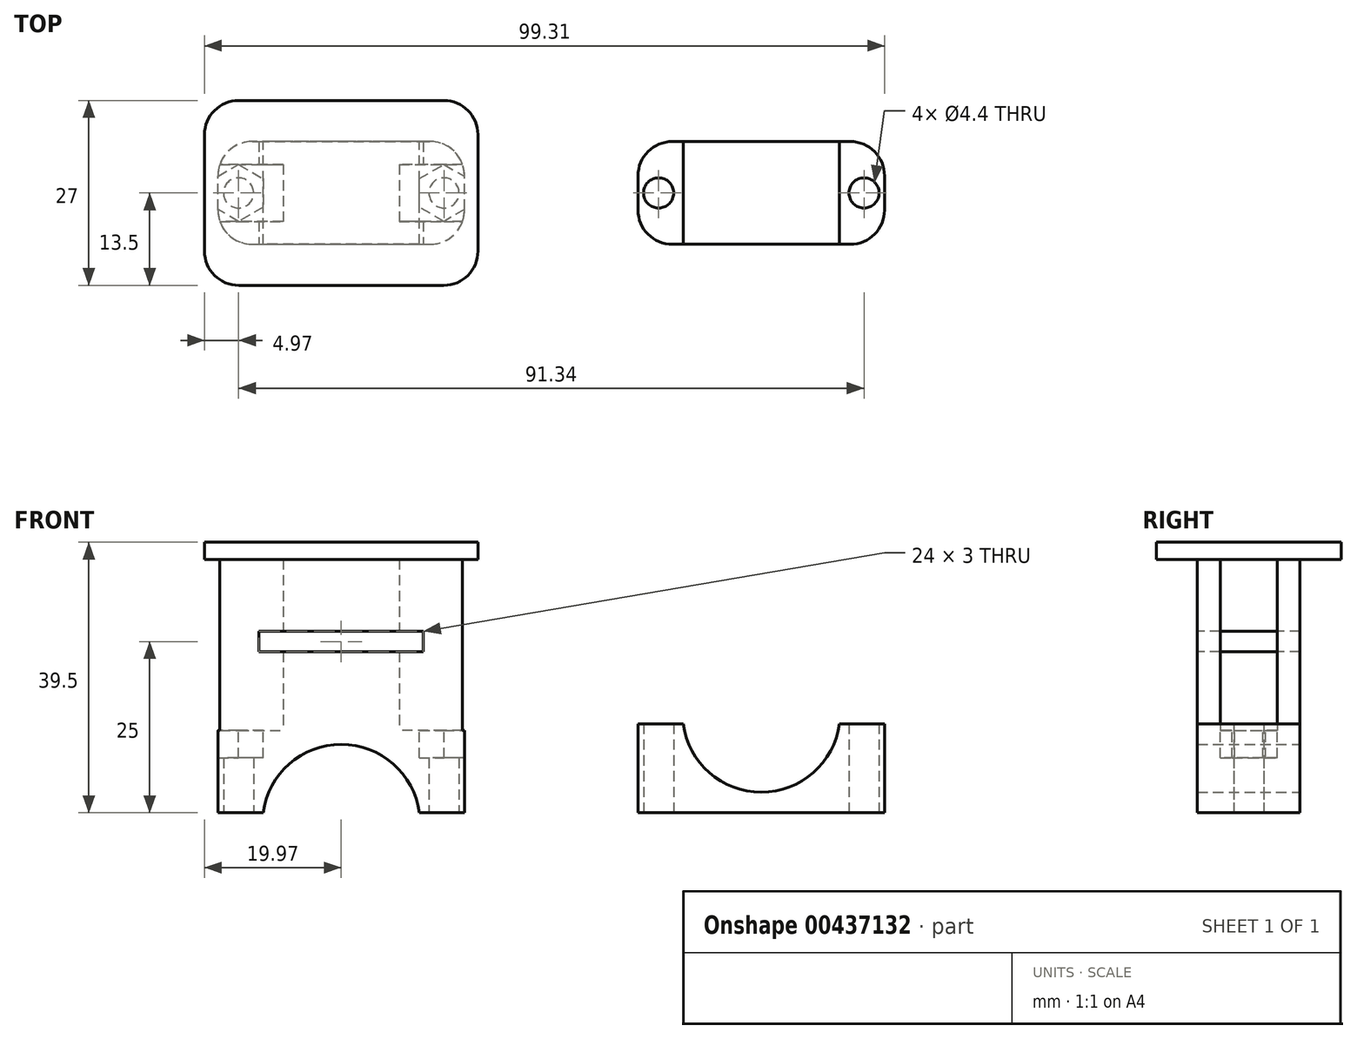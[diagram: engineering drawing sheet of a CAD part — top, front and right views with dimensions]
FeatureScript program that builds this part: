
annotation { "Feature Type Name" : "Feature", "Feature Type Description" : "" }
export const myFeature = defineFeature(function(context is Context, id is Id, definition is map)
    precondition{}
    {
        {
            var Q0;
            Q0=qCreatedBy(makeId("Front.planeOp"),FACE);
            var sketch = newSketch(context, id + "F0", { "sketchPlane" : qUnion([Q0])});
            skLineSegment(sketch, "E0.bottom", {"start": v(0, 0) * mm, "end": v(36, 0) * mm});
            skLineSegment(sketch, "E0.top", {"start": v(0, 13) * mm, "end": v(36, 13) * mm});
            skLineSegment(sketch, "E0.left", {"start": v(0, 0) * mm, "end": v(0, 13) * mm});
            skLineSegment(sketch, "E0.right", {"start": v(36, 0) * mm, "end": v(36, 13) * mm});
            skPoint(sketch, "E1", {"position": v(18, 14.5) * mm});
            skPoint(sketch, "E1.positionSnap0", {"position": v(18, 13) * mm});
            skCircle(sketch, "E2", {"center": v(18, 14.5) * mm, "radius": 11.5 * mm});
            skSolve(sketch);
        }
        {
            var Q0;
            Q0=makeQuery(id+"F0.imprint","IMPRINT",FACE,{"disambiguationData":[TD([[makeQuery(id+"F0.imprint","IMPRINT",EDGE,{"derivedFrom":sQuery(id+"F0.wireOp",EDGE,"E0.bottom")}),1.0]])]});
            extrude(context, id + "F1", {"entities" : qUnion([Q0]), "depth" : 15 * mm});
        }
        {
            var Q0;
            Q0=makeQuery(id+"F1.opExtrude","CAP_EDGE",EDGE,{"disambiguationData":[OSD([sQuery(id+"F0.wireOp",EDGE,"E0.left")])],"isStart":false});
            var Q1;
            Q1=makeQuery(id+"F1.opExtrude","CAP_EDGE",EDGE,{"disambiguationData":[OSD([sQuery(id+"F0.wireOp",EDGE,"E0.right")])],"isStart":false});
            var Q2;
            Q2=makeQuery(id+"F1.opExtrude","CAP_EDGE",EDGE,{"disambiguationData":[OSD([sQuery(id+"F0.wireOp",EDGE,"E0.right")])],"isStart":true});
            var Q3;
            Q3=makeQuery(id+"F1.opExtrude","CAP_EDGE",EDGE,{"disambiguationData":[OSD([sQuery(id+"F0.wireOp",EDGE,"E0.left")])],"isStart":true});
            fillet(context, id + "F2", {"entities" : qUnion([Q0, Q1, Q2, Q3]), "radius" : 5 * mm, "tangentPropagation" : true, "allowEdgeOverflow" : false});
        }
        {
            var Q0;
            Q0=makeQuery(id+"F1.opExtrude","SWEPT_FACE",FACE,{"disambiguationData":[OSD([sQuery(id+"F0.wireOp",EDGE,"E0.bottom")])]});
            var sketch = newSketch(context, id + "F3", { "sketchPlane" : qUnion([Q0])});
            skPoint(sketch, "E3", {"position": v(3, 7.5) * mm});
            skPoint(sketch, "E3.positionSnap0", {"position": v(0, 7.5) * mm});
            skPoint(sketch, "E4", {"position": v(36, 7.5) * mm});
            skPoint(sketch, "E5", {"position": v(33, 7.5) * mm});
            skCircle(sketch, "E6", {"center": v(3, 7.5) * mm, "radius": 2.2 * mm});
            skCircle(sketch, "E7", {"center": v(33, 7.5) * mm, "radius": 2.2 * mm});
            skSolve(sketch);
        }
        {
            var Q0;
            Q0 = qSketchRegion(id + "F3", true);
            extrude(context, id + "F4", {"entities" : qUnion([Q0]), "operationType" : NewBodyOperationType.REMOVE, "oppositeDirection" : true, "depth" : 25 * mm});
        }
        {
            var Q0;
            Q0=qCreatedBy(makeId("Front.planeOp"),FACE);
            var sketch = newSketch(context, id + "F5", { "sketchPlane" : qUnion([Q0])});
            skLineSegment(sketch, "E8.bottom", {"start": v(-61.34, 0) * mm, "end": v(-25.34, 0) * mm});
            skLineSegment(sketch, "E8.top", {"start": v(-61.34, 12) * mm, "end": v(-25.34, 12) * mm});
            skLineSegment(sketch, "E8.left", {"start": v(-61.34, 0) * mm, "end": v(-61.34, 12) * mm});
            skLineSegment(sketch, "E8.right", {"start": v(-25.34, 0) * mm, "end": v(-25.34, 12) * mm});
            skPoint(sketch, "E9", {"position": v(-43.34, -1.5) * mm});
            skPoint(sketch, "E9.positionSnap0", {"position": v(-43.34, 0) * mm});
            skCircle(sketch, "E10", {"center": v(-43.34, -1.5) * mm, "radius": 11.5 * mm});
            skPoint(sketch, "E11", {"position": v(-43.34, 12) * mm});
            skPoint(sketch, "E12", {"position": v(-51.8, 12) * mm});
            skLineSegment(sketch, "E13", {"start": v(-43.34, 12) * mm, "end": v(-43.34, 15.53) * mm, "construction": true});
            skLineSegment(sketch, "E14", {"start": v(-51.8, 12) * mm, "end": v(-51.8, 37) * mm});
            skLineSegment(sketch, "E15.MirrorCS", {"start": v(-34.87, 12) * mm, "end": v(-34.87, 37) * mm});
            skLineSegment(sketch, "E16", {"start": v(-51.8, 37) * mm, "end": v(-34.87, 37) * mm});
            skLineSegment(sketch, "E17", {"start": v(-51.8, 37) * mm, "end": v(-63.3, 37) * mm});
            skLineSegment(sketch, "E18", {"start": v(-34.87, 37) * mm, "end": v(-23.37, 37) * mm});
            skLineSegment(sketch, "E19", {"start": v(-63.3, 37) * mm, "end": v(-63.3, 39.5) * mm});
            skLineSegment(sketch, "E20", {"start": v(-63.3, 39.5) * mm, "end": v(-23.37, 39.5) * mm});
            skLineSegment(sketch, "E21", {"start": v(-23.37, 39.5) * mm, "end": v(-23.37, 37) * mm});
            skSolve(sketch);
        }
        {
            var Q0;
            {var subQ3=sQuery(id+"F5.wireOp",EDGE,"E8.left");Q0=makeQuery(id+"F5.imprint","IMPRINT",FACE,{"disambiguationData":[TD([[makeQuery(id+"F5.imprint","IMPRINT",EDGE,{"derivedFrom":subQ3}),-1.0]])]});}
            var Q1;
            {var subQ0=sQuery(id+"F5.wireOp",EDGE,"E14");Q1=makeQuery(id+"F5.imprint","IMPRINT",FACE,{"disambiguationData":[TD([[makeQuery(id+"F5.imprint","IMPRINT",EDGE,{"derivedFrom":subQ0}),-1.0]])]});}
            extrude(context, id + "F6", {"entities" : qUnion([Q0, Q1]), "depth" : 15 * mm});
        }
        {
            var Q0;
            Q0=makeQuery(id+"F5.imprint","IMPRINT",FACE,{"disambiguationData":[TD([[makeQuery(id+"F5.imprint","IMPRINT",EDGE,{"derivedFrom":sQuery(id+"F5.wireOp",EDGE,"E16")}),1.0]])]});
            extrude(context, id + "F7", {"entities" : qUnion([Q0]), "operationType" : NewBodyOperationType.ADD, "depth" : 21 * mm});
        }
        {
            var Q0;
            Q0=makeQuery(id+"F5.imprint","IMPRINT",FACE,{"disambiguationData":[TD([[makeQuery(id+"F5.imprint","IMPRINT",EDGE,{"derivedFrom":sQuery(id+"F5.wireOp",EDGE,"E16")}),1.0]])]});
            extrude(context, id + "F8", {"entities" : qUnion([Q0]), "operationType" : NewBodyOperationType.ADD, "oppositeDirection" : true, "depth" : 6 * mm});
        }
        {
            var Q0;
            Q0=makeQuery(id+"F6.opExtrude","CAP_EDGE",EDGE,{"disambiguationData":[OSD([sQuery(id+"F5.wireOp",EDGE,"E8.right")])],"isStart":false});
            var Q1;
            Q1=makeQuery(id+"F6.opExtrude","CAP_EDGE",EDGE,{"disambiguationData":[OSD([sQuery(id+"F5.wireOp",EDGE,"E8.right")])],"isStart":true});
            var Q2;
            Q2=makeQuery(id+"F6.opExtrude","CAP_EDGE",EDGE,{"disambiguationData":[OSD([sQuery(id+"F5.wireOp",EDGE,"E8.left")])],"isStart":false});
            var Q3;
            Q3=makeQuery(id+"F6.opExtrude","CAP_EDGE",EDGE,{"disambiguationData":[OSD([sQuery(id+"F5.wireOp",EDGE,"E8.left")])],"isStart":true});
            fillet(context, id + "F9", {"entities" : qUnion([Q0, Q1, Q2, Q3]), "radius" : 5 * mm, "tangentPropagation" : true, "allowEdgeOverflow" : false});
        }
        {
            var Q0;
            {var subQ0=sQuery(id+"F5.wireOp",EDGE,"E8.bottom");Q0=makeQuery(id+"F6.opExtrude","SWEPT_FACE",FACE,{"disambiguationData":[OSD([subQ0]),TDD([makeQuery(id+"F5.imprint","IMPRINT",EDGE,{"disambiguationData":[TD([[makeQuery(id+"F5.imprint","INTERSECT",VERTEX,{"derivedFrom":[subQ0,sQuery(id+"F5.wireOp",EDGE,"E8.left")]}),-1.0]])],"derivedFrom":subQ0})])]});}
            var sketch = newSketch(context, id + "F10", { "sketchPlane" : qUnion([Q0])});
            skPoint(sketch, "E22", {"position": v(-58.34, 7.5) * mm});
            skPoint(sketch, "E22.positionSnap0", {"position": v(-61.34, 7.5) * mm});
            skCircle(sketch, "E23", {"center": v(-58.34, 7.5) * mm, "radius": 2.2 * mm});
            skSolve(sketch);
        }
        {
            var Q0;
            {var subQ0=sQuery(id+"F5.wireOp",EDGE,"E8.bottom");Q0=makeQuery(id+"F6.opExtrude","SWEPT_FACE",FACE,{"disambiguationData":[OSD([subQ0]),TDD([makeQuery(id+"F5.imprint","IMPRINT",EDGE,{"disambiguationData":[TD([[makeQuery(id+"F5.imprint","INTERSECT",VERTEX,{"derivedFrom":[subQ0,sQuery(id+"F5.wireOp",EDGE,"E8.right")]}),1.0]])],"derivedFrom":subQ0})])]});}
            var sketch = newSketch(context, id + "F11", { "sketchPlane" : qUnion([Q0])});
            skPoint(sketch, "E24", {"position": v(-28.34, 7.5) * mm});
            skPoint(sketch, "E24.positionSnap0", {"position": v(-25.34, 7.5) * mm});
            skCircle(sketch, "E25", {"center": v(-28.34, 7.5) * mm, "radius": 2.2 * mm});
            skSolve(sketch);
        }
        {
            var Q0;
            Q0=makeQuery(id+"F10.imprint","IMPRINT",FACE,{"disambiguationData":[TD([[makeQuery(id+"F10.imprint","IMPRINT",EDGE,{"derivedFrom":sQuery(id+"F10.wireOp",EDGE,"E23")}),1.0]])]});
            var Q1;
            Q1=makeQuery(id+"F11.imprint","IMPRINT",FACE,{"disambiguationData":[TD([[makeQuery(id+"F11.imprint","IMPRINT",EDGE,{"derivedFrom":sQuery(id+"F11.wireOp",EDGE,"E25")}),1.0]])]});
            extrude(context, id + "F12", {"entities" : qUnion([Q0, Q1]), "operationType" : NewBodyOperationType.REMOVE, "oppositeDirection" : true, "depth" : 25 * mm});
        }
        {
            var Q0;
            {var subQ0=sQuery(id+"F5.wireOp",EDGE,"E8.top");Q0=makeQuery(id+"F6.opExtrude","SWEPT_FACE",FACE,{"disambiguationData":[OSD([subQ0]),TDD([makeQuery(id+"F5.imprint","IMPRINT",EDGE,{"disambiguationData":[TD([[makeQuery(id+"F5.imprint","INTERSECT",VERTEX,{"derivedFrom":[subQ0,sQuery(id+"F5.wireOp",EDGE,"E8.left")]}),-1.0]])],"derivedFrom":subQ0})])]});}
            var sketch = newSketch(context, id + "F13", { "sketchPlane" : qUnion([Q0])});
            skCircle(sketch, "E26.cCircle", {"center": v(-58.34, -7.5) * mm, "radius": 3.6 * mm, "construction": true});
            skLineSegment(sketch, "E26.0", {"start": v(-61.94, -9.58) * mm, "end": v(-61.94, -5.42) * mm});
            skLineSegment(sketch, "E26.1", {"start": v(-61.94, -5.42) * mm, "end": v(-58.34, -3.34) * mm});
            skLineSegment(sketch, "E26.2", {"start": v(-58.34, -3.34) * mm, "end": v(-54.74, -5.42) * mm});
            skLineSegment(sketch, "E26.3", {"start": v(-54.74, -5.42) * mm, "end": v(-54.74, -9.58) * mm});
            skLineSegment(sketch, "E26.4", {"start": v(-54.74, -9.58) * mm, "end": v(-58.34, -11.66) * mm});
            skLineSegment(sketch, "E26.5", {"start": v(-58.34, -11.66) * mm, "end": v(-61.94, -9.58) * mm});
            skPoint(sketch, "E26.0.midPoint", {"position": v(-61.94, -7.5) * mm});
            skLineSegment(sketch, "E27", {"start": v(-58.34, -3.34) * mm, "end": v(-51.8, -3.34) * mm});
            skLineSegment(sketch, "E28", {"start": v(-58.34, -11.66) * mm, "end": v(-51.8, -11.66) * mm});
            skLineSegment(sketch, "E29", {"start": v(-58.34, -3.34) * mm, "end": v(-61.06, -3.34) * mm});
            skLineSegment(sketch, "E30", {"start": v(-58.34, -11.66) * mm, "end": v(-61.06, -11.66) * mm});
            skSolve(sketch);
        }
        {
            var Q0;
            {var subQ8=sQuery(id+"F13.wireOp",EDGE,"E26.2");Q0=makeQuery(id+"F13.imprint","IMPRINT",FACE,{"disambiguationData":[TD([[makeQuery(id+"F13.imprint","IMPRINT",EDGE,{"derivedFrom":subQ8}),-1.0]])]});}
            extrude(context, id + "F14", {"entities" : qUnion([Q0]), "operationType" : NewBodyOperationType.REMOVE, "oppositeDirection" : true, "depth" : 4 * mm});
        }
        {
            var Q0;
            {var subQ0=sQuery(id+"F5.wireOp",EDGE,"E8.top");Q0=makeQuery(id+"F6.opExtrude","SWEPT_FACE",FACE,{"disambiguationData":[OSD([subQ0]),TDD([makeQuery(id+"F5.imprint","IMPRINT",EDGE,{"disambiguationData":[TD([[makeQuery(id+"F5.imprint","INTERSECT",VERTEX,{"derivedFrom":[subQ0,sQuery(id+"F5.wireOp",EDGE,"E8.right")]}),1.0]])],"derivedFrom":subQ0})])]});}
            var sketch = newSketch(context, id + "F15", { "sketchPlane" : qUnion([Q0])});
            skCircle(sketch, "E31.cCircle", {"center": v(-28.34, -7.5) * mm, "radius": 3.6 * mm, "construction": true});
            skPoint(sketch, "E31.cCircle.perimeterSnap0", {"position": v(-25.34, -7.5) * mm});
            skLineSegment(sketch, "E31.0", {"start": v(-24.74, -5.42) * mm, "end": v(-24.74, -9.58) * mm});
            skLineSegment(sketch, "E31.1", {"start": v(-24.74, -9.58) * mm, "end": v(-28.34, -11.66) * mm});
            skLineSegment(sketch, "E31.2", {"start": v(-28.34, -11.66) * mm, "end": v(-31.94, -9.58) * mm});
            skLineSegment(sketch, "E31.3", {"start": v(-31.94, -9.58) * mm, "end": v(-31.94, -5.42) * mm});
            skLineSegment(sketch, "E31.4", {"start": v(-31.94, -5.42) * mm, "end": v(-28.34, -3.34) * mm});
            skLineSegment(sketch, "E31.5", {"start": v(-28.34, -3.34) * mm, "end": v(-24.74, -5.42) * mm});
            skPoint(sketch, "E31.0.midPoint", {"position": v(-24.74, -7.5) * mm});
            skPoint(sketch, "E31.0.midPoint.positionSnap0", {"position": v(-25.34, -7.5) * mm});
            skLineSegment(sketch, "E32", {"start": v(-28.34, -11.66) * mm, "end": v(-34.87, -11.66) * mm});
            skLineSegment(sketch, "E33", {"start": v(-28.34, -11.66) * mm, "end": v(-25.62, -11.66) * mm});
            skLineSegment(sketch, "E34", {"start": v(-28.34, -3.34) * mm, "end": v(-34.87, -3.34) * mm});
            skLineSegment(sketch, "E35", {"start": v(-28.34, -3.34) * mm, "end": v(-25.62, -3.34) * mm});
            skSolve(sketch);
        }
        {
            var Q0;
            {var subQ1=sQuery(id+"F15.wireOp",EDGE,"E31.2");Q0=makeQuery(id+"F15.imprint","IMPRINT",FACE,{"disambiguationData":[TD([[makeQuery(id+"F15.imprint","IMPRINT",EDGE,{"derivedFrom":subQ1}),-1.0]])]});}
            extrude(context, id + "F16", {"entities" : qUnion([Q0]), "operationType" : NewBodyOperationType.REMOVE, "oppositeDirection" : true, "depth" : 4 * mm});
        }
        {
            var Q0;
            {var subQ6=sQuery(id+"F13.wireOp",EDGE,"E28");Q0=makeQuery(id+"F13.imprint","IMPRINT",FACE,{"disambiguationData":[TD([[makeQuery(id+"F13.imprint","IMPRINT",EDGE,{"derivedFrom":subQ6}),-1.0]])]});}
            var Q1;
            {var subQ6=sQuery(id+"F13.wireOp",EDGE,"E27");Q1=makeQuery(id+"F13.imprint","IMPRINT",FACE,{"disambiguationData":[TD([[makeQuery(id+"F13.imprint","IMPRINT",EDGE,{"derivedFrom":subQ6}),1.0]])]});}
            var Q2;
            {var subQ6=sQuery(id+"F15.wireOp",EDGE,"E32");Q2=makeQuery(id+"F15.imprint","IMPRINT",FACE,{"disambiguationData":[TD([[makeQuery(id+"F15.imprint","IMPRINT",EDGE,{"derivedFrom":subQ6}),1.0]])]});}
            var Q3;
            {var subQ8=sQuery(id+"F15.wireOp",EDGE,"E34");Q3=makeQuery(id+"F15.imprint","IMPRINT",FACE,{"disambiguationData":[TD([[makeQuery(id+"F15.imprint","IMPRINT",EDGE,{"derivedFrom":subQ8}),-1.0]])]});}
            extrude(context, id + "F17", {"entities" : qUnion([Q0, Q1, Q2, Q3]), "operationType" : NewBodyOperationType.ADD, "endBound" : BoundingType.UP_TO_NEXT, "depth" : 25 * mm});
        }
        {
            var Q0;
            Q0=makeQuery(id+"F7.opExtrude","CAP_EDGE",EDGE,{"disambiguationData":[OSD([sQuery(id+"F5.wireOp",EDGE,"E21")])],"isStart":false});
            var Q1;
            Q1=makeQuery(id+"F8.opExtrude","CAP_EDGE",EDGE,{"disambiguationData":[OSD([sQuery(id+"F5.wireOp",EDGE,"E21")])],"isStart":false});
            var Q2;
            Q2=makeQuery(id+"F8.opExtrude","CAP_EDGE",EDGE,{"disambiguationData":[OSD([sQuery(id+"F5.wireOp",EDGE,"E19")])],"isStart":false});
            var Q3;
            Q3=makeQuery(id+"F7.opExtrude","CAP_EDGE",EDGE,{"disambiguationData":[OSD([sQuery(id+"F5.wireOp",EDGE,"E19")])],"isStart":false});
            fillet(context, id + "F18", {"entities" : qUnion([Q0, Q1, Q2, Q3]), "radius" : 5 * mm, "tangentPropagation" : true, "allowEdgeOverflow" : false});
        }
        {
            var Q0;
            {var subQ0=sQuery(id+"F5.wireOp",EDGE,"E8.right");var subQ1=sQuery(id+"F5.wireOp",EDGE,"E8.top");var subQ2=sQuery(id+"F5.wireOp",EDGE,"E15.MirrorCS");var subQ3=sQuery(id+"F5.wireOp",EDGE,"E8.left");var subQ4=sQuery(id+"F5.wireOp",EDGE,"E14");Q0=makeQuery(id+"F17.boolean.opBoolean","MERGE",FACE,{"derivedFrom":[makeQuery(id+"F6.opExtrude","CAP_FACE",FACE,{"disambiguationData":[OSD([sQuery(id+"F5.wireOp",EDGE,"E8.bottom"),subQ1,subQ3,subQ0,sQuery(id+"F5.wireOp",EDGE,"E10"),subQ4,subQ2,sQuery(id+"F5.wireOp",EDGE,"E16")])],"isStart":false}),makeQuery(id+"F17.opExtrude","SWEPT_FACE",FACE,{"disambiguationData":[OSD([subQ1]),TDD([makeQuery(id+"F13.imprint","IMPRINT",EDGE,{"derivedFrom":makeQuery(id+"F6.opExtrude","CAP_EDGE",EDGE,{"disambiguationData":[OSD([subQ1]),TDD([makeQuery(id+"F5.imprint","IMPRINT",EDGE,{"disambiguationData":[TD([[makeQuery(id+"F5.imprint","INTERSECT",VERTEX,{"derivedFrom":[subQ1,subQ3]}),-1.0]])],"derivedFrom":subQ1})])],"isStart":false})})])]}),makeQuery(id+"F17.opExtrude","SWEPT_FACE",FACE,{"disambiguationData":[OSD([subQ1]),TDD([makeQuery(id+"F15.imprint","IMPRINT",EDGE,{"derivedFrom":makeQuery(id+"F6.opExtrude","CAP_EDGE",EDGE,{"disambiguationData":[OSD([subQ1]),TDD([makeQuery(id+"F5.imprint","IMPRINT",EDGE,{"disambiguationData":[TD([[makeQuery(id+"F5.imprint","INTERSECT",VERTEX,{"derivedFrom":[subQ1,subQ0]}),1.0]])],"derivedFrom":subQ1})])],"isStart":false})})])]})]});}
            var sketch = newSketch(context, id + "F19", { "sketchPlane" : qUnion([Q0])});
            skPoint(sketch, "E36", {"position": v(-43.34, 25) * mm});
            skPoint(sketch, "E36.positionSnap0", {"position": v(-43.34, 37) * mm});
            skLineSegment(sketch, "E37.bottom", {"start": v(-55.34, 23.5) * mm, "end": v(-31.34, 23.5) * mm});
            skLineSegment(sketch, "E37.top", {"start": v(-55.34, 26.5) * mm, "end": v(-31.34, 26.5) * mm});
            skLineSegment(sketch, "E37.left", {"start": v(-55.34, 23.5) * mm, "end": v(-55.34, 26.5) * mm});
            skLineSegment(sketch, "E37.right", {"start": v(-31.34, 23.5) * mm, "end": v(-31.34, 26.5) * mm});
            skSolve(sketch);
        }
        {
            var Q0;
            Q0=makeQuery(id+"F19.imprint","IMPRINT",FACE,{"disambiguationData":[TD([[makeQuery(id+"F19.imprint","IMPRINT",EDGE,{"derivedFrom":sQuery(id+"F19.wireOp",EDGE,"E37.bottom")}),1.0]])]});
            extrude(context, id + "F20", {"entities" : qUnion([Q0]), "operationType" : NewBodyOperationType.REMOVE, "oppositeDirection" : true, "depth" : 25 * mm});
        }
    });
